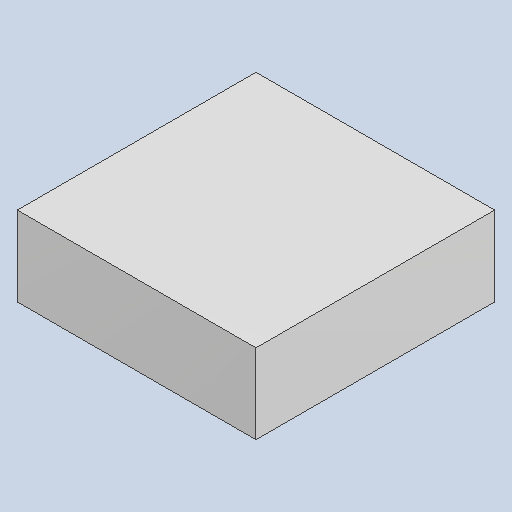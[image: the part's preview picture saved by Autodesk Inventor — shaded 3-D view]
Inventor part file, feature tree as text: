
AUTODESK INVENTOR PART (.ipt)
format: ipt  version: 2023.4 (Build 274418000, 418)  size: 79,872 bytes
history: native  units: mm
features: extrude x1
ambient origin geometry x8: Origin, YZ Plane, XZ Plane, XY Plane, X Axis, Y Axis, Z Axis, Center Point
bodies: Solid1 (feature_tree)
feature tree (1):
  extrude  "Extruded_47"  [1 undecoded]
note: 1 required parameter value undecoded (feature->parameter linkage not recoverable at this tier; creation-order binding heuristic only, values carry confidence <= 0.55)
